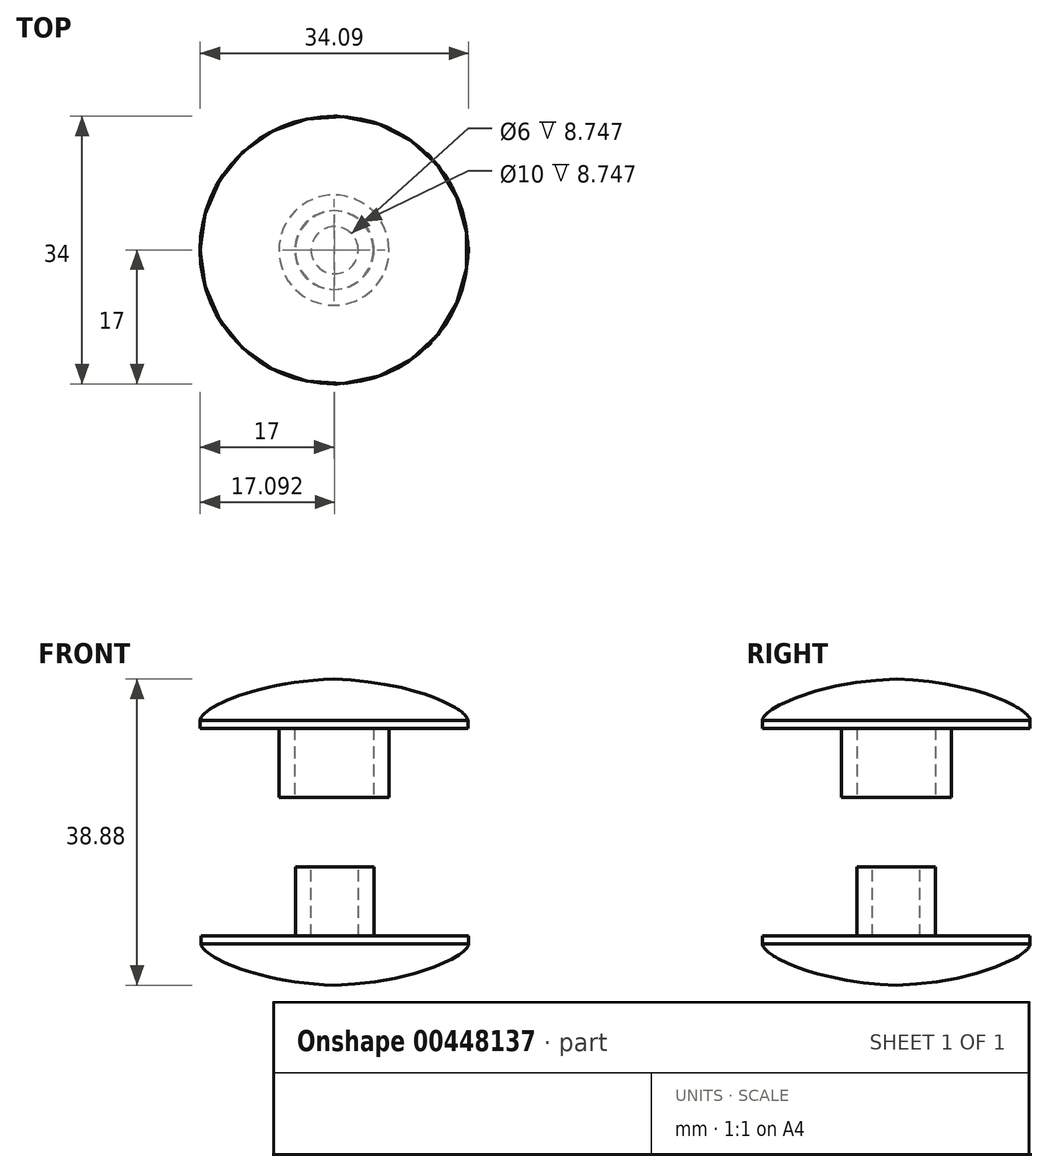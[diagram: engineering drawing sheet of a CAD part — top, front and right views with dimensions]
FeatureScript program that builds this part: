
annotation { "Feature Type Name" : "Feature", "Feature Type Description" : "" }
export const myFeature = defineFeature(function(context is Context, id is Id, definition is map)
    precondition{}
    {
        {
            var Q0;
            Q0=qCreatedBy(makeId("Front.planeOp"),FACE);
            var sketch = newSketch(context, id + "F0", { "sketchPlane" : qUnion([Q0])});
            skLineSegment(sketch, "E0", {"start": v(0, 0) * mm, "end": v(0, 6.21) * mm});
            skFitSpline(sketch, "E1", {"points": [v(-17, 0.96) * mm, v(0, 6.21) * mm], "startDerivative": vector(-0.15, 4.22) * mm, "endDerivative": vector(31.22, 1.02) * mm});
            skLineSegment(sketch, "E2", {"start": v(-17, 0.96) * mm, "end": v(-17, -0.04) * mm});
            skLineSegment(sketch, "E3", {"start": v(-17, -0.04) * mm, "end": v(-7, -0.04) * mm});
            skLineSegment(sketch, "E4", {"start": v(-7, -0.04) * mm, "end": v(-7, -8.8) * mm});
            skLineSegment(sketch, "E5", {"start": v(-7, -8.8) * mm, "end": v(-5, -8.8) * mm});
            skLineSegment(sketch, "E6", {"start": v(-5, -8.8) * mm, "end": v(-5, -0.04) * mm});
            skLineSegment(sketch, "E7", {"start": v(-5, -0.04) * mm, "end": v(0, -0.04) * mm});
            skLineSegment(sketch, "E8", {"start": v(0, -0.04) * mm, "end": v(0, 0) * mm});
            skSolve(sketch);
        }
        {
            var Q0;
            Q0=makeQuery(id+"F0.imprint","IMPRINT",FACE,{"disambiguationData":[TD([[makeQuery(id+"F0.imprint","IMPRINT",EDGE,{"derivedFrom":sQuery(id+"F0.wireOp",EDGE,"E0")}),1.0]])]});
            var Q1;
            Q1=sQuery(id+"F0.wireOp",EDGE,"E0");
            revolve(context, id + "F1", {"entities" : qUnion([Q0]), "axis" : qUnion([Q1]), "revolveType" : RevolveType.FULL});
        }
        {
            var Q0;
            Q0=qCreatedBy(makeId("Front.planeOp"),FACE);
            var sketch = newSketch(context, id + "F2", { "sketchPlane" : qUnion([Q0])});
            skLineSegment(sketch, "E9", {"start": v(-4.9, -17.66) * mm, "end": v(-2.9, -17.66) * mm});
            skLineSegment(sketch, "E10.MirrorCS", {"start": v(-16.9, -27.41) * mm, "end": v(-16.9, -26.41) * mm});
            skLineSegment(sketch, "E11.MirrorCS", {"start": v(0.1, -26.41) * mm, "end": v(0.1, -32.67) * mm});
            skFitSpline(sketch, "E12.MirrorCS", {"points": [v(-16.9, -27.41) * mm, v(0.1, -32.67) * mm], "startDerivative": vector(-0.15, -4.22) * mm, "endDerivative": vector(31.22, -1.02) * mm});
            skLineSegment(sketch, "E13.MirrorCS", {"start": v(-16.9, -26.41) * mm, "end": v(-4.9, -26.41) * mm});
            skLineSegment(sketch, "E14.MirrorCS", {"start": v(-4.9, -26.41) * mm, "end": v(-4.9, -17.66) * mm});
            skLineSegment(sketch, "E15.MirrorCS", {"start": v(-2.9, -26.41) * mm, "end": v(0.1, -26.41) * mm});
            skLineSegment(sketch, "E16.MirrorCS", {"start": v(-2.9, -17.66) * mm, "end": v(-2.9, -26.41) * mm});
            skLineSegment(sketch, "E17", {"start": v(0.1, -26.41) * mm, "end": v(0.1, -26.41) * mm});
            skSolve(sketch);
        }
        {
            var Q0;
            Q0=makeQuery(id+"F2.imprint","IMPRINT",FACE,{"disambiguationData":[TD([[makeQuery(id+"F2.imprint","IMPRINT",EDGE,{"derivedFrom":sQuery(id+"F2.wireOp",EDGE,"E9")}),-1.0]])]});
            var Q1;
            Q1=sQuery(id+"F2.wireOp",EDGE,"E11.MirrorCS");
            revolve(context, id + "F3", {"entities" : qUnion([Q0]), "axis" : qUnion([Q1]), "revolveType" : RevolveType.FULL});
        }
    });
